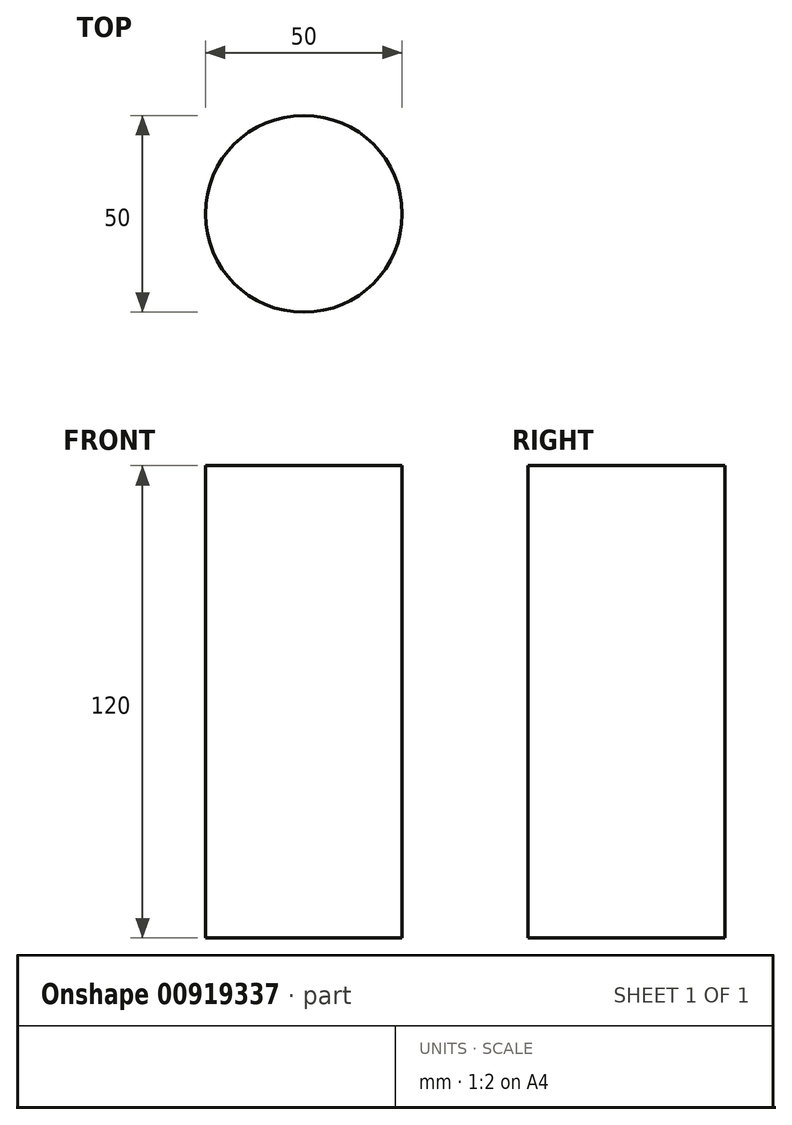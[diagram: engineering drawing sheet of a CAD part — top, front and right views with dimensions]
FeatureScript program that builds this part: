
annotation { "Feature Type Name" : "Feature", "Feature Type Description" : "" }
export const myFeature = defineFeature(function(context is Context, id is Id, definition is map)
    precondition{}
    {
        {
            var Q0;
            Q0=qCreatedBy(makeId("Top.planeOp"),FACE);
            var sketch = newSketch(context, id + "F0", { "sketchPlane" : qUnion([Q0])});
            skCircle(sketch, "E0", {"center": v(0, 0) * mm, "radius": 25 * mm});
            skSolve(sketch);
        }
        {
            var Q0;
            Q0 = qSketchRegion(id + "F0", true);
            extrude(context, id + "F1", {"entities" : qUnion([Q0]), "depth" : 120 * mm, "offsetDistance" : 25 * mm});
        }
    });
